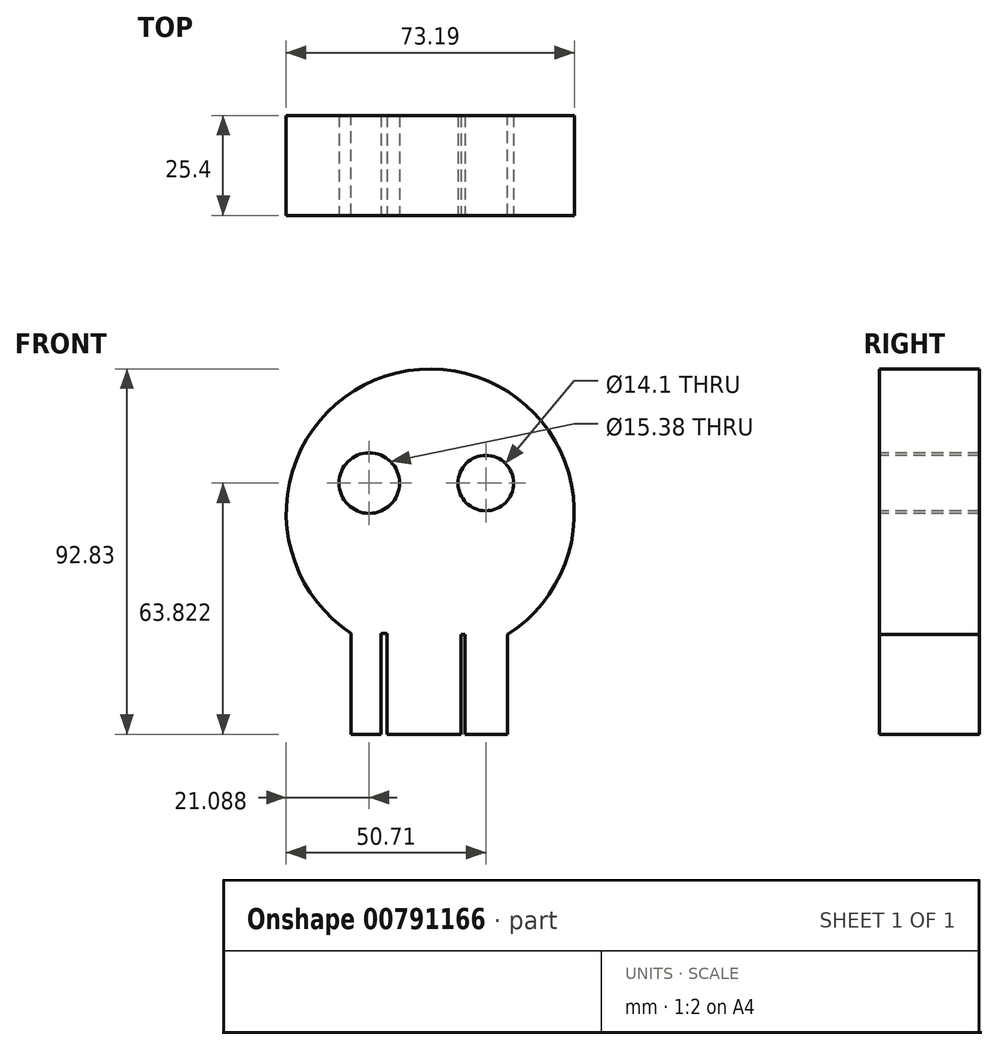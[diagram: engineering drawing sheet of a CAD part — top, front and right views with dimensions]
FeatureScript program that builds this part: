
annotation { "Feature Type Name" : "Feature", "Feature Type Description" : "" }
export const myFeature = defineFeature(function(context is Context, id is Id, definition is map)
    precondition{}
    {
        {
            var Q0;
            Q0=qCreatedBy(makeId("Front.planeOp"),FACE);
            var sketch = newSketch(context, id + "F0", { "sketchPlane" : qUnion([Q0])});
            skArc(sketch, "E0", {"start": v(19.7, -11.15) * mm, "mid": v(0.37, 56.34) * mm, "end": v(-20, -10.84) * mm});
            skLineSegment(sketch, "E1", {"start": v(-20, -10.84) * mm, "end": v(-20, -36.5) * mm});
            skLineSegment(sketch, "E2", {"start": v(-20, -36.5) * mm, "end": v(-7.48, -36.5) * mm});
            skLineSegment(sketch, "E3", {"start": v(-7.48, -36.5) * mm, "end": v(-7.48, -10.84) * mm});
            skLineSegment(sketch, "E4", {"start": v(-7.48, -36.5) * mm, "end": v(6.87, -36.5) * mm});
            skLineSegment(sketch, "E5", {"start": v(6.87, -36.5) * mm, "end": v(6.87, -10.84) * mm});
            skLineSegment(sketch, "E6", {"start": v(6.87, -36.5) * mm, "end": v(19.7, -36.5) * mm});
            skLineSegment(sketch, "E7", {"start": v(19.7, -36.5) * mm, "end": v(19.7, -11.15) * mm});
            skSolve(sketch);
        }
        {
            var Q0;
            Q0=makeQuery(id+"F0.imprint","IMPRINT",FACE,{"disambiguationData":[TD([[makeQuery(id+"F0.imprint","IMPRINT",EDGE,{"derivedFrom":sQuery(id+"F0.wireOp",EDGE,"E0")}),1.0]])]});
            extrude(context, id + "F1", {"entities" : qUnion([Q0]), "depth" : 25.4 * mm, "offsetDistance" : 25.4 * mm});
        }
        {
            var Q0;
            Q0=makeQuery(id+"F1.opExtrude","CAP_FACE",FACE,{"disambiguationData":[OSD([sQuery(id+"F0.wireOp",EDGE,"E0"),sQuery(id+"F0.wireOp",EDGE,"E1"),sQuery(id+"F0.wireOp",EDGE,"E2"),sQuery(id+"F0.wireOp",EDGE,"E4"),sQuery(id+"F0.wireOp",EDGE,"E6"),sQuery(id+"F0.wireOp",EDGE,"E7")])],"isStart":false});
            var sketch = newSketch(context, id + "F2", { "sketchPlane" : qUnion([Q0])});
            skLineSegment(sketch, "E8.bottom", {"start": v(-12.4, -10.84) * mm, "end": v(-10.9, -10.84) * mm});
            skLineSegment(sketch, "E8.top", {"start": v(-12.4, -36.5) * mm, "end": v(-10.9, -36.5) * mm});
            skLineSegment(sketch, "E8.left", {"start": v(-12.4, -10.84) * mm, "end": v(-12.4, -36.5) * mm});
            skLineSegment(sketch, "E8.right", {"start": v(-10.9, -10.84) * mm, "end": v(-10.9, -36.5) * mm});
            skLineSegment(sketch, "E9.bottom", {"start": v(8.94, -11.15) * mm, "end": v(7.95, -11.15) * mm});
            skLineSegment(sketch, "E9.top", {"start": v(8.94, -36.5) * mm, "end": v(7.95, -36.5) * mm});
            skLineSegment(sketch, "E9.left", {"start": v(8.94, -11.15) * mm, "end": v(8.94, -36.5) * mm});
            skLineSegment(sketch, "E9.right", {"start": v(7.95, -11.15) * mm, "end": v(7.95, -36.5) * mm});
            skSolve(sketch);
        }
        {
            var Q0;
            Q0=makeQuery(id+"F2.imprint","IMPRINT",FACE,{"disambiguationData":[TD([[makeQuery(id+"F2.imprint","IMPRINT",EDGE,{"derivedFrom":sQuery(id+"F2.wireOp",EDGE,"E8.bottom")}),-1.0]])]});
            var Q1;
            Q1=makeQuery(id+"F2.imprint","IMPRINT",FACE,{"disambiguationData":[TD([[makeQuery(id+"F2.imprint","IMPRINT",EDGE,{"derivedFrom":sQuery(id+"F2.wireOp",EDGE,"E9.bottom")}),1.0]])]});
            extrude(context, id + "F3", {"entities" : qUnion([Q0, Q1]), "operationType" : NewBodyOperationType.REMOVE, "oppositeDirection" : true, "depth" : 25.4 * mm, "offsetDistance" : 25.4 * mm});
        }
        {
            var Q0;
            Q0=makeQuery(id+"F1.opExtrude","CAP_FACE",FACE,{"disambiguationData":[OSD([sQuery(id+"F0.wireOp",EDGE,"E0"),sQuery(id+"F0.wireOp",EDGE,"E1"),sQuery(id+"F0.wireOp",EDGE,"E2"),sQuery(id+"F0.wireOp",EDGE,"E4"),sQuery(id+"F0.wireOp",EDGE,"E6"),sQuery(id+"F0.wireOp",EDGE,"E7")])],"isStart":false});
            var sketch = newSketch(context, id + "F4", { "sketchPlane" : qUnion([Q0])});
            skCircle(sketch, "E10", {"center": v(-15.42, 27.33) * mm, "radius": 7.69 * mm});
            skCircle(sketch, "E11", {"center": v(14.2, 27.33) * mm, "radius": 7.05 * mm});
            skSolve(sketch);
        }
        {
            var Q0;
            Q0=makeQuery(id+"F4.imprint","IMPRINT",FACE,{"disambiguationData":[TD([[makeQuery(id+"F4.imprint","IMPRINT",EDGE,{"derivedFrom":sQuery(id+"F4.wireOp",EDGE,"E10")}),1.0]])]});
            var Q1;
            Q1=makeQuery(id+"F4.imprint","IMPRINT",FACE,{"disambiguationData":[TD([[makeQuery(id+"F4.imprint","IMPRINT",EDGE,{"derivedFrom":sQuery(id+"F4.wireOp",EDGE,"E11")}),1.0]])]});
            extrude(context, id + "F5", {"entities" : qUnion([Q0, Q1]), "operationType" : NewBodyOperationType.REMOVE, "oppositeDirection" : true, "depth" : 25.4 * mm, "offsetDistance" : 25.4 * mm});
        }
    });
